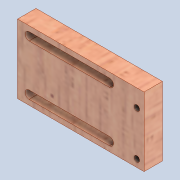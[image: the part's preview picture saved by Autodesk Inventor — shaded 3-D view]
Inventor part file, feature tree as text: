
AUTODESK INVENTOR PART (.ipt)
format: ipt  version: 2020 (Build 240168000, 168)  size: 201,216 bytes
history: native  units: mm
features: extrude x2, sketch x2, hole x1
ambient origin geometry x8: Origin, YZ Plane, XZ Plane, XY Plane, X Axis, Y Axis, Z Axis, Center Point
bodies: Solid1 (feature_tree)
feature tree (5):
  extrude  "Extrusion1"  Depth=30.0mm
  extrude  "Extrusion5"  Depth=3.5mm
  hole  "Hole1"  [1 undecoded]
  sketch  "Sketch1"  dims[d0=55.0mm d1=30.0mm]
  sketch  "Sketch5"  dims[d2=8.0mm d3=0.0mm d29=3.5mm d30=4.0mm d31=4.0mm d33=35.0mm d34=10.0mm d35=0.0mm d36=5.0mm d37=2.459mm d38=8.0mm d39=4.0mm d40=2.0mm d41=90.0deg d42=8.0mm d43=20.594885mm d44=3.1275mm]
note: 1 required parameter value undecoded (feature->parameter linkage not recoverable at this tier; creation-order binding heuristic only, values carry confidence <= 0.55)
